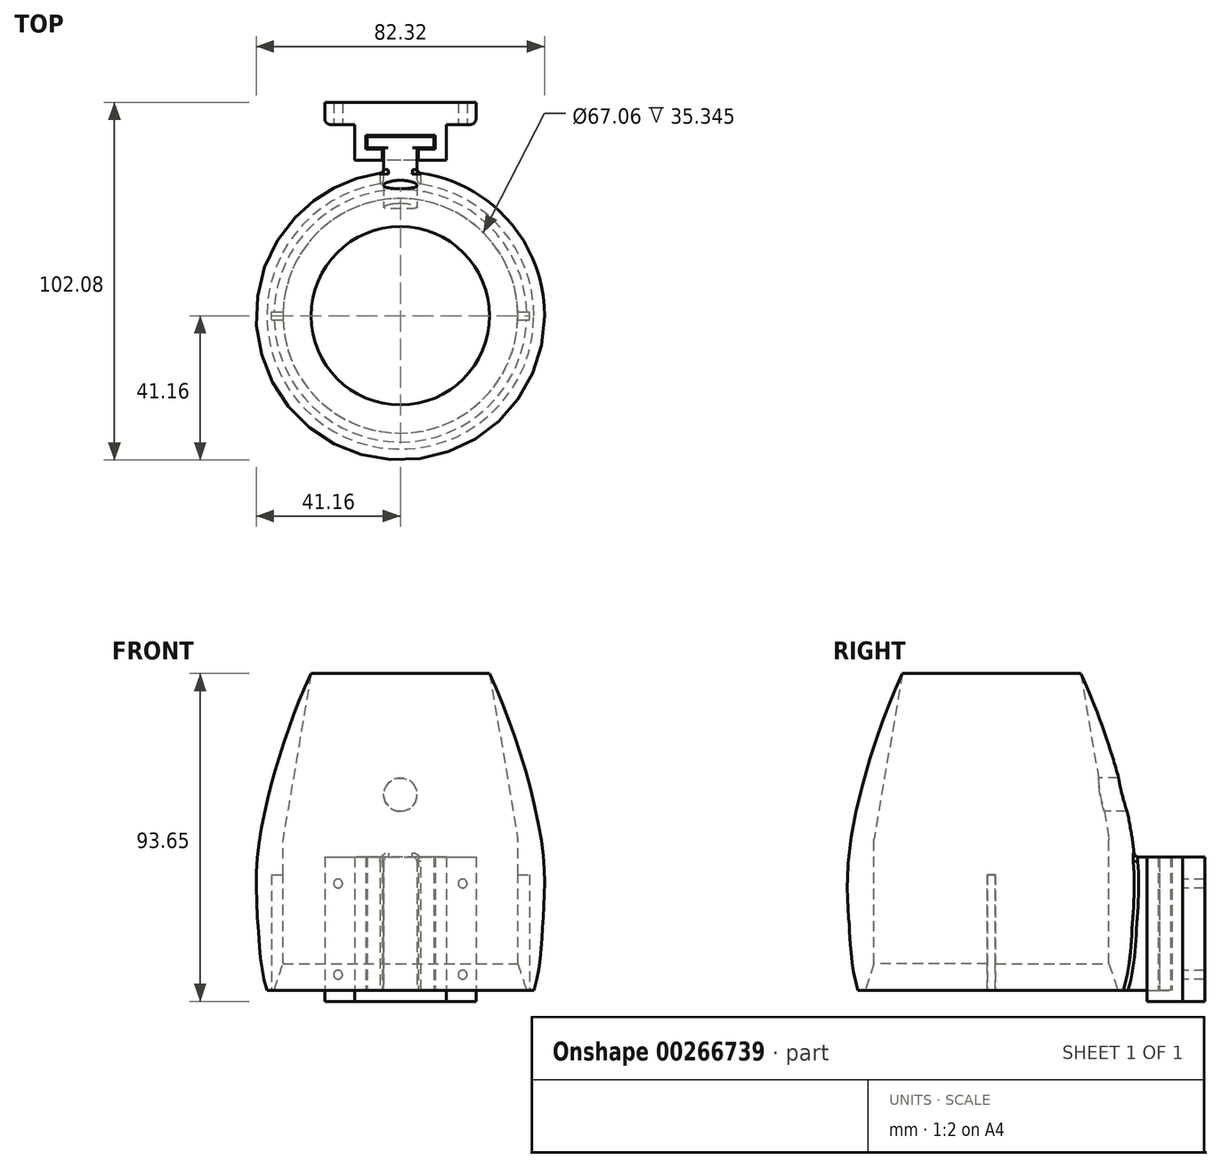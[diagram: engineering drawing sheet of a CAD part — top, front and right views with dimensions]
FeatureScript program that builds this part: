
annotation { "Feature Type Name" : "Feature", "Feature Type Description" : "" }
export const myFeature = defineFeature(function(context is Context, id is Id, definition is map)
    precondition{}
    {
        {
            var Q0;
            Q0=qCreatedBy(makeId("Front.planeOp"),FACE);
            var sketch = newSketch(context, id + "F0", { "sketchPlane" : qUnion([Q0])});
            skLineSegment(sketch, "E0", {"start": v(33.53, 0) * mm, "end": v(33.53, 43.18) * mm});
            skFitSpline(sketch, "E1", {"points": [v(25.48, 90.48) * mm, v(40.22, 42.95) * mm, v(40.56, 17.78) * mm, v(38.1, 0) * mm], "startDerivative": vector(40.31, -83.9) * mm, "endDerivative": vector(-21.68, -71.3) * mm});
            skLineSegment(sketch, "E2", {"start": v(38.1, 0) * mm, "end": v(33.53, 0) * mm});
            skLineSegment(sketch, "E3", {"start": v(0, 45.2) * mm, "end": v(0, -33.23) * mm, "construction": true});
            skLineSegment(sketch, "E4", {"start": v(33.53, 43.18) * mm, "end": v(25.48, 90.48) * mm});
            skSolve(sketch);
        }
        {
            var Q0;
            Q0=makeQuery(id+"F0.imprint","IMPRINT",FACE,{"disambiguationData":[TD([[makeQuery(id+"F0.imprint","IMPRINT",EDGE,{"derivedFrom":sQuery(id+"F0.wireOp",EDGE,"E0")}),-1.0]])]});
            var Q1;
            Q1=sQuery(id+"F0.wireOp",EDGE,"E3");
            revolve(context, id + "F1", {"entities" : qUnion([Q0]), "axis" : qUnion([Q1]), "revolveType" : RevolveType.FULL});
        }
        {
            var Q0;
            Q0=makeQuery(id+"F1.opRevolve","SWEPT_FACE",FACE,{"disambiguationData":[OSD([sQuery(id+"F0.wireOp",EDGE,"E2")])]});
            var sketch = newSketch(context, id + "F2", { "sketchPlane" : qUnion([Q0])});
            skLineSegment(sketch, "E5.bottom", {"start": v(-4.76, -37.8) * mm, "end": v(4.76, -37.8) * mm});
            skLineSegment(sketch, "E5.top", {"start": v(-4.76, -47.96) * mm, "end": v(4.76, -47.96) * mm});
            skLineSegment(sketch, "E5.left", {"start": v(-4.76, -37.8) * mm, "end": v(-4.76, -47.96) * mm});
            skLineSegment(sketch, "E5.right", {"start": v(4.76, -37.8) * mm, "end": v(4.76, -47.96) * mm});
            skSolve(sketch);
        }
        {
            var Q0;
            Q0=makeQuery(id+"F2.imprint","IMPRINT",FACE,{"disambiguationData":[TD([[makeQuery(id+"F2.imprint","IMPRINT",EDGE,{"derivedFrom":sQuery(id+"F2.wireOp",EDGE,"E5.top")}),1.0]])]});
            extrude(context, id + "F3", {"entities" : qUnion([Q0]), "operationType" : NewBodyOperationType.ADD, "oppositeDirection" : true, "depth" : 38.1 * mm});
        }
        {
            var Q0;
            Q0=makeQuery(id+"F3.opExtrude","SWEPT_FACE",FACE,{"disambiguationData":[OSD([sQuery(id+"F2.wireOp",EDGE,"E5.top")])]});
            var sketch = newSketch(context, id + "F4", { "sketchPlane" : qUnion([Q0])});
            skLineSegment(sketch, "E6.bottom", {"start": v(-9.52, 38.1) * mm, "end": v(9.53, 38.1) * mm});
            skLineSegment(sketch, "E6.top", {"start": v(-9.52, 0) * mm, "end": v(9.53, 0) * mm});
            skLineSegment(sketch, "E6.left", {"start": v(-9.52, 38.1) * mm, "end": v(-9.52, 0) * mm});
            skLineSegment(sketch, "E6.right", {"start": v(9.53, 38.1) * mm, "end": v(9.53, 0) * mm});
            skSolve(sketch);
        }
        {
            var Q0;
            Q0 = qSketchRegion(id + "F4", true);
            extrude(context, id + "F5", {"entities" : qUnion([Q0]), "operationType" : NewBodyOperationType.ADD, "depth" : 3.17 * mm});
        }
        {
            var Q0;
            Q0=makeQuery(id+"F3.boolean.opBoolean","INTERSECT",EDGE,{"derivedFrom":[makeQuery(id+"F1.opRevolve","SWEPT_FACE",FACE,{"disambiguationData":[OSD([sQuery(id+"F0.wireOp",EDGE,"E1")])]}),makeQuery(id+"F3.opExtrude","SWEPT_FACE",FACE,{"disambiguationData":[OSD([sQuery(id+"F2.wireOp",EDGE,"E5.left")])]})]});
            var Q1;
            {var subQ0=sQuery(id+"F0.wireOp",EDGE,"E1");Q1=makeQuery(id+"F3.boolean.opBoolean","INTERSECT",EDGE,{"derivedFrom":[makeQuery(id+"F1.opRevolve","SWEPT_FACE",FACE,{"disambiguationData":[OSD([subQ0])]}),makeQuery(id+"F3.opExtrude","CAP_FACE",FACE,{"disambiguationData":[OSD([subQ0,sQuery(id+"F0.wireOp",EDGE,"E2"),sQuery(id+"F2.wireOp",EDGE,"E5.top"),sQuery(id+"F2.wireOp",EDGE,"E5.left"),sQuery(id+"F2.wireOp",EDGE,"E5.right")])],"isStart":false})]});}
            var Q2;
            Q2=makeQuery(id+"F3.boolean.opBoolean","INTERSECT",EDGE,{"derivedFrom":[makeQuery(id+"F1.opRevolve","SWEPT_FACE",FACE,{"disambiguationData":[OSD([sQuery(id+"F0.wireOp",EDGE,"E1")])]}),makeQuery(id+"F3.opExtrude","SWEPT_FACE",FACE,{"disambiguationData":[OSD([sQuery(id+"F2.wireOp",EDGE,"E5.right")])]})]});
            var Q3;
            Q3=makeQuery(id+"F3.opExtrude","CAP_EDGE",EDGE,{"disambiguationData":[OSD([sQuery(id+"F2.wireOp",EDGE,"E5.right")])],"isStart":false});
            var Q4;
            Q4=makeQuery(id+"F3.opExtrude","CAP_EDGE",EDGE,{"disambiguationData":[OSD([sQuery(id+"F2.wireOp",EDGE,"E5.left")])],"isStart":false});
            fillet(context, id + "F6", {"entities" : qUnion([Q0, Q1, Q2, Q3, Q4]), "radius" : 1.27 * mm, "tangentPropagation" : true, "allowEdgeOverflow" : false});
        }
        {
            var Q0;
            Q0=qCreatedBy(makeId("Top.planeOp"),FACE);
            var sketch = newSketch(context, id + "F7", { "sketchPlane" : qUnion([Q0])});
            skLineSegment(sketch, "E7", {"start": v(-5.14, 44.4) * mm, "end": v(-13.08, 44.4) * mm});
            skLineSegment(sketch, "E8", {"start": v(-13.08, 44.4) * mm, "end": v(-13.08, 54.57) * mm});
            skLineSegment(sketch, "E9", {"start": v(-13.08, 54.57) * mm, "end": v(13.08, 54.57) * mm});
            skLineSegment(sketch, "E10", {"start": v(13.08, 54.57) * mm, "end": v(13.08, 44.4) * mm});
            skLineSegment(sketch, "E11", {"start": v(13.08, 44.4) * mm, "end": v(5.14, 44.4) * mm});
            skLineSegment(sketch, "E12", {"start": v(5.14, 44.4) * mm, "end": v(5.14, 47.58) * mm});
            skLineSegment(sketch, "E13", {"start": v(5.14, 47.58) * mm, "end": v(9.9, 47.58) * mm});
            skLineSegment(sketch, "E14", {"start": v(9.9, 47.58) * mm, "end": v(9.9, 51.52) * mm});
            skLineSegment(sketch, "E15", {"start": v(9.9, 51.52) * mm, "end": v(-9.9, 51.52) * mm});
            skLineSegment(sketch, "E16", {"start": v(-9.9, 51.52) * mm, "end": v(-9.9, 47.58) * mm});
            skLineSegment(sketch, "E17", {"start": v(-9.9, 47.58) * mm, "end": v(-5.14, 47.58) * mm});
            skLineSegment(sketch, "E18", {"start": v(-5.14, 47.58) * mm, "end": v(-5.14, 44.4) * mm});
            skSolve(sketch);
        }
        {
            var Q0;
            Q0 = qSketchRegion(id + "F7", true);
            extrude(context, id + "F8", {"entities" : qUnion([Q0]), "depth" : 38.1 * mm});
        }
        {
            var Q0;
            Q0=makeQuery(id+"F8.opExtrude","CAP_FACE",FACE,{"disambiguationData":[OSD([sQuery(id+"F7.wireOp",EDGE,"E7"),sQuery(id+"F7.wireOp",EDGE,"E8"),sQuery(id+"F7.wireOp",EDGE,"E9"),sQuery(id+"F7.wireOp",EDGE,"E10"),sQuery(id+"F7.wireOp",EDGE,"E11"),sQuery(id+"F7.wireOp",EDGE,"E12"),sQuery(id+"F7.wireOp",EDGE,"E13"),sQuery(id+"F7.wireOp",EDGE,"E14"),sQuery(id+"F7.wireOp",EDGE,"E15"),sQuery(id+"F7.wireOp",EDGE,"E16"),sQuery(id+"F7.wireOp",EDGE,"E17"),sQuery(id+"F7.wireOp",EDGE,"E18")])],"isStart":true});
            var sketch = newSketch(context, id + "F9", { "sketchPlane" : qUnion([Q0])});
            skLineSegment(sketch, "E19.bottom", {"start": v(-13.08, -54.57) * mm, "end": v(13.08, -54.57) * mm});
            skLineSegment(sketch, "E19.top", {"start": v(-13.08, -44.4) * mm, "end": v(13.08, -44.4) * mm});
            skLineSegment(sketch, "E19.left", {"start": v(-13.08, -54.57) * mm, "end": v(-13.08, -44.4) * mm});
            skLineSegment(sketch, "E19.right", {"start": v(13.08, -54.57) * mm, "end": v(13.08, -44.4) * mm});
            skSolve(sketch);
        }
        {
            var Q0;
            Q0 = qSketchRegion(id + "F9", true);
            extrude(context, id + "F10", {"entities" : qUnion([Q0]), "operationType" : NewBodyOperationType.ADD, "depth" : 3.17 * mm});
        }
        {
            var Q0;
            Q0=makeQuery(id+"F10.opExtrude","CAP_FACE",FACE,{"disambiguationData":[OSD([sQuery(id+"F9.wireOp",EDGE,"E19.bottom"),sQuery(id+"F9.wireOp",EDGE,"E19.top"),sQuery(id+"F9.wireOp",EDGE,"E19.left"),sQuery(id+"F9.wireOp",EDGE,"E19.right")])],"isStart":false});
            var sketch = newSketch(context, id + "F11", { "sketchPlane" : qUnion([Q0])});
            skLineSegment(sketch, "E20.bottom", {"start": v(-21.59, -54.57) * mm, "end": v(21.6, -54.57) * mm});
            skLineSegment(sketch, "E20.top", {"start": v(-21.59, -60.92) * mm, "end": v(21.59, -60.92) * mm});
            skLineSegment(sketch, "E20.left", {"start": v(-21.59, -54.57) * mm, "end": v(-21.59, -60.92) * mm});
            skLineSegment(sketch, "E20.right", {"start": v(21.59, -54.57) * mm, "end": v(21.59, -60.92) * mm});
            skSolve(sketch);
        }
        {
            var Q0;
            Q0 = qSketchRegion(id + "F11", true);
            var Q1;
            Q1=makeQuery(id+"F8.opExtrude","CAP_FACE",FACE,{"disambiguationData":[OSD([sQuery(id+"F7.wireOp",EDGE,"E7"),sQuery(id+"F7.wireOp",EDGE,"E8"),sQuery(id+"F7.wireOp",EDGE,"E9"),sQuery(id+"F7.wireOp",EDGE,"E10"),sQuery(id+"F7.wireOp",EDGE,"E11"),sQuery(id+"F7.wireOp",EDGE,"E12"),sQuery(id+"F7.wireOp",EDGE,"E13"),sQuery(id+"F7.wireOp",EDGE,"E14"),sQuery(id+"F7.wireOp",EDGE,"E15"),sQuery(id+"F7.wireOp",EDGE,"E16"),sQuery(id+"F7.wireOp",EDGE,"E17"),sQuery(id+"F7.wireOp",EDGE,"E18")])],"isStart":false});
            extrude(context, id + "F12", {"entities" : qUnion([Q0]), "operationType" : NewBodyOperationType.ADD, "endBound" : BoundingType.UP_TO_SURFACE, "oppositeDirection" : true, "endBoundEntityFace" : qUnion([Q1]), "depth" : 25.4 * mm});
        }
        {
            var Q0;
            Q0=makeQuery(id+"F10.boolean.opBoolean","MERGE",EDGE,{"derivedFrom":[makeQuery(id+"F8.opExtrude","SWEPT_EDGE",EDGE,{"disambiguationData":[OSD([sQuery(id+"F7.wireOp",EDGE,"E9"),sQuery(id+"F7.wireOp",EDGE,"E10")])]}),makeQuery(id+"F10.opExtrude","SWEPT_EDGE",EDGE,{"disambiguationData":[OSD([sQuery(id+"F9.wireOp",EDGE,"E19.bottom"),sQuery(id+"F9.wireOp",EDGE,"E19.right")])]})]});
            var Q1;
            Q1=makeQuery(id+"F12.opExtrude","SWEPT_EDGE",EDGE,{"disambiguationData":[OSD([sQuery(id+"F11.wireOp",EDGE,"E20.bottom"),sQuery(id+"F11.wireOp",EDGE,"E20.right")])]});
            var Q2;
            Q2=makeQuery(id+"F10.boolean.opBoolean","MERGE",EDGE,{"derivedFrom":[makeQuery(id+"F8.opExtrude","SWEPT_EDGE",EDGE,{"disambiguationData":[OSD([sQuery(id+"F7.wireOp",EDGE,"E8"),sQuery(id+"F7.wireOp",EDGE,"E9")])]}),makeQuery(id+"F10.opExtrude","SWEPT_EDGE",EDGE,{"disambiguationData":[OSD([sQuery(id+"F9.wireOp",EDGE,"E19.bottom"),sQuery(id+"F9.wireOp",EDGE,"E19.left")])]})]});
            var Q3;
            Q3=makeQuery(id+"F12.opExtrude","SWEPT_EDGE",EDGE,{"disambiguationData":[OSD([sQuery(id+"F11.wireOp",EDGE,"E20.bottom"),sQuery(id+"F11.wireOp",EDGE,"E20.left")])]});
            fillet(context, id + "F13", {"entities" : qUnion([Q0, Q1, Q2, Q3]), "radius" : 1.78 * mm, "tangentPropagation" : true, "allowEdgeOverflow" : false});
        }
        {
            var Q0;
            {var subQ1=sQuery(id+"F7.wireOp",EDGE,"E8");var subQ14=sQuery(id+"F11.wireOp",EDGE,"E20.bottom");Q0=makeQuery(id+"F12.boolean.opBoolean","SPLIT",FACE,{"disambiguationData":[TD([makeQuery(id+"F8.opExtrude","SWEPT_FACE",FACE,{"disambiguationData":[OSD([subQ1])]})])],"derivedFrom":makeQuery(id+"F12.opExtrude","SWEPT_FACE",FACE,{"disambiguationData":[OSD([subQ14])]})});}
            var sketch = newSketch(context, id + "F14", { "sketchPlane" : qUnion([Q0])});
            skCircle(sketch, "E21", {"center": v(-17.78, 30.48) * mm, "radius": 1.27 * mm});
            skPoint(sketch, "E21.centerSnap0", {"position": v(-17.78, 38.1) * mm});
            skCircle(sketch, "E22", {"center": v(-17.78, 4.44) * mm, "radius": 1.27 * mm});
            skCircle(sketch, "E23", {"center": v(17.78, 30.48) * mm, "radius": 1.27 * mm});
            skCircle(sketch, "E24", {"center": v(17.78, 4.44) * mm, "radius": 1.27 * mm});
            skSolve(sketch);
        }
        {
            var Q0;
            Q0 = qSketchRegion(id + "F14", true);
            extrude(context, id + "F15", {"entities" : qUnion([Q0]), "operationType" : NewBodyOperationType.REMOVE, "endBound" : BoundingType.THROUGH_ALL, "oppositeDirection" : true, "depth" : 25.4 * mm});
        }
        {
            var Q0;
            Q0=makeQuery(id+"F1.opRevolve","SWEPT_EDGE",EDGE,{"disambiguationData":[OSD([sQuery(id+"F0.wireOp",EDGE,"E0"),sQuery(id+"F0.wireOp",EDGE,"E2")])]});
            chamfer(context, id + "F16", {"entities" : qUnion([Q0]), "chamferType" : ChamferType.TWO_OFFSETS, "width1" : 2.54 * mm, "oppositeDirection" : false, "width2" : 7.62 * mm, "tangentPropagation" : true});
        }
        {
            var Q0;
            Q0=qCreatedBy(makeId("Top.planeOp"),FACE);
            var sketch = newSketch(context, id + "F17", { "sketchPlane" : qUnion([Q0])});
            skLineSegment(sketch, "E25.bottom", {"start": v(-36.83, -1.14) * mm, "end": v(36.83, -1.14) * mm});
            skLineSegment(sketch, "E25.top", {"start": v(-36.83, 1.14) * mm, "end": v(36.83, 1.14) * mm});
            skLineSegment(sketch, "E25.left", {"start": v(-36.83, -1.14) * mm, "end": v(-36.83, 1.14) * mm});
            skLineSegment(sketch, "E25.right", {"start": v(36.83, -1.14) * mm, "end": v(36.83, 1.14) * mm});
            skSolve(sketch);
        }
        {
            var Q0;
            Q0 = qSketchRegion(id + "F17", true);
            extrude(context, id + "F18", {"entities" : qUnion([Q0]), "operationType" : NewBodyOperationType.REMOVE, "depth" : 33.02 * mm});
        }
        {
            var Q0;
            Q0=qCreatedBy(makeId("Front.planeOp"),FACE);
            var sketch = newSketch(context, id + "F19", { "sketchPlane" : qUnion([Q0])});
            skCircle(sketch, "E26", {"center": v(0, 55.88) * mm, "radius": 4.76 * mm});
            skSolve(sketch);
        }
        {
            var Q0;
            Q0 = qSketchRegion(id + "F19", true);
            var Q1;
            Q1=sQuery(id+"F19.wireOp",EDGE,"E26");
            extrude(context, id + "F20", {"entities" : qUnion([Q0]), "operationType" : NewBodyOperationType.REMOVE, "surfaceEntities" : qUnion([Q1]), "endBound" : BoundingType.THROUGH_ALL, "oppositeDirection" : true, "depth" : 25.4 * mm});
        }
        {
            var Q0;
            Q0=makeQuery(id+"F1.opRevolve","SWEPT_EDGE",EDGE,{"disambiguationData":[OSD([sQuery(id+"F0.wireOp",EDGE,"E0"),sQuery(id+"F0.wireOp",EDGE,"E4")])]});
            fillet(context, id + "F21", {"entities" : qUnion([Q0]), "radius" : 2.54 * mm, "tangentPropagation" : true, "allowEdgeOverflow" : false});
        }
    });
